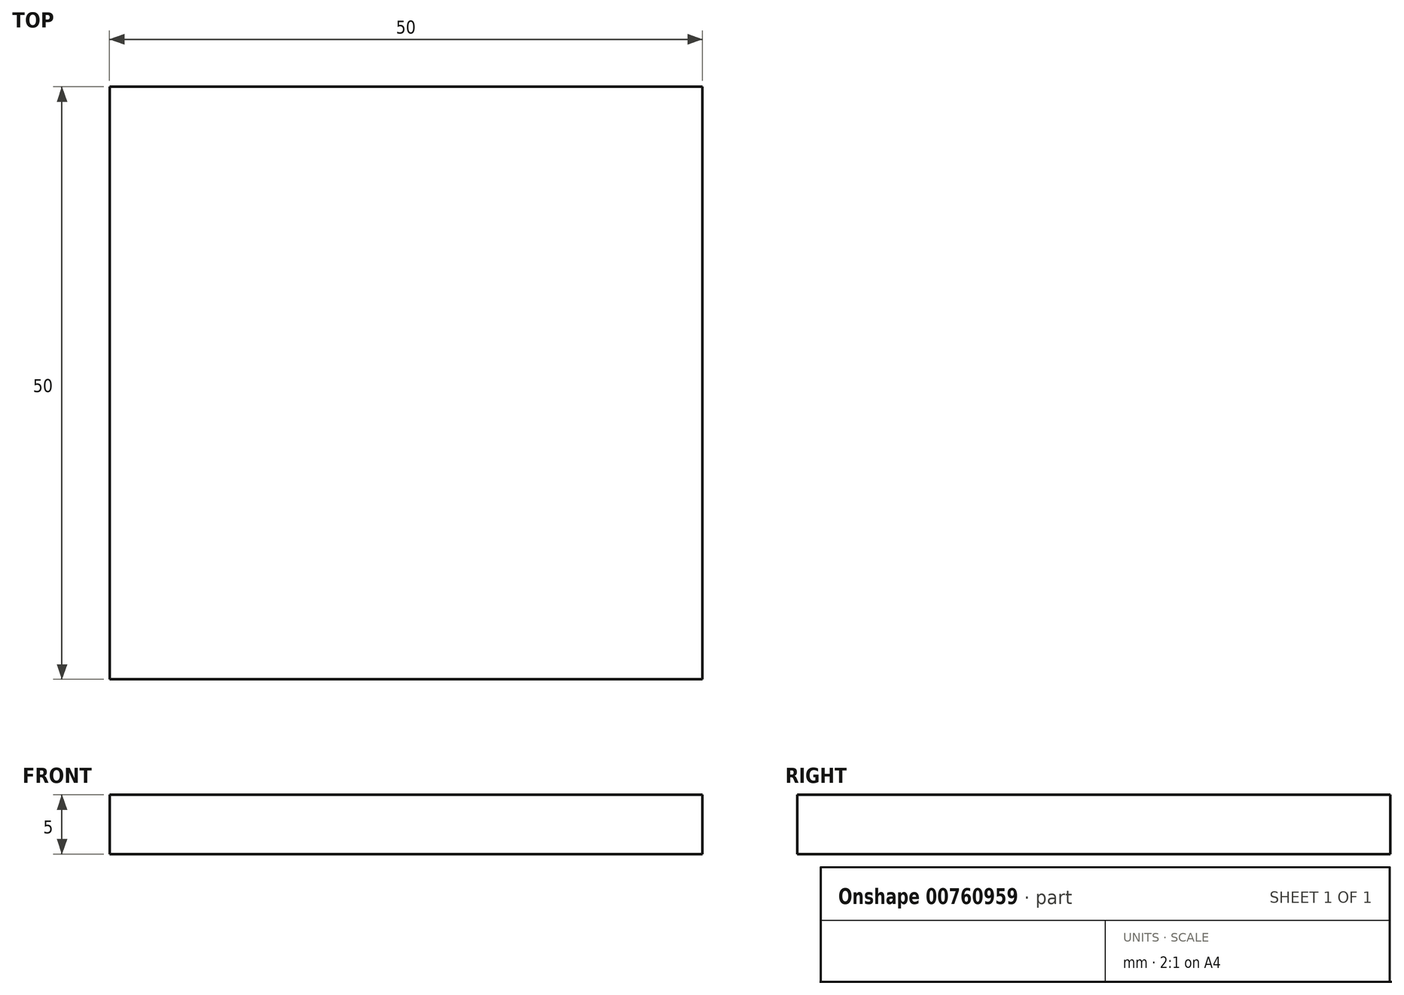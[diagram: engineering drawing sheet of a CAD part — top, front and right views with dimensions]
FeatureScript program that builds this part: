
annotation { "Feature Type Name" : "Feature", "Feature Type Description" : "" }
export const myFeature = defineFeature(function(context is Context, id is Id, definition is map)
    precondition{}
    {
        {
            var Q0;
            Q0=qCreatedBy(makeId("Top.planeOp"),FACE);
            var sketch = newSketch(context, id + "F0", { "sketchPlane" : qUnion([Q0])});
            skLineSegment(sketch, "E0.bottom", {"start": v(-24.03, 24.84) * mm, "end": v(25.97, 24.84) * mm});
            skLineSegment(sketch, "E0.top", {"start": v(-24.03, -25.16) * mm, "end": v(25.97, -25.16) * mm});
            skLineSegment(sketch, "E0.left", {"start": v(-24.03, 24.84) * mm, "end": v(-24.03, -25.16) * mm});
            skLineSegment(sketch, "E0.right", {"start": v(25.97, 24.84) * mm, "end": v(25.97, -25.16) * mm});
            skSolve(sketch);
        }
        {
            var Q0;
            Q0 = qSketchRegion(id + "F0", true);
            extrude(context, id + "F1", {"entities" : qUnion([Q0]), "depth" : 5 * mm, "offsetDistance" : 25 * mm});
        }
    });
